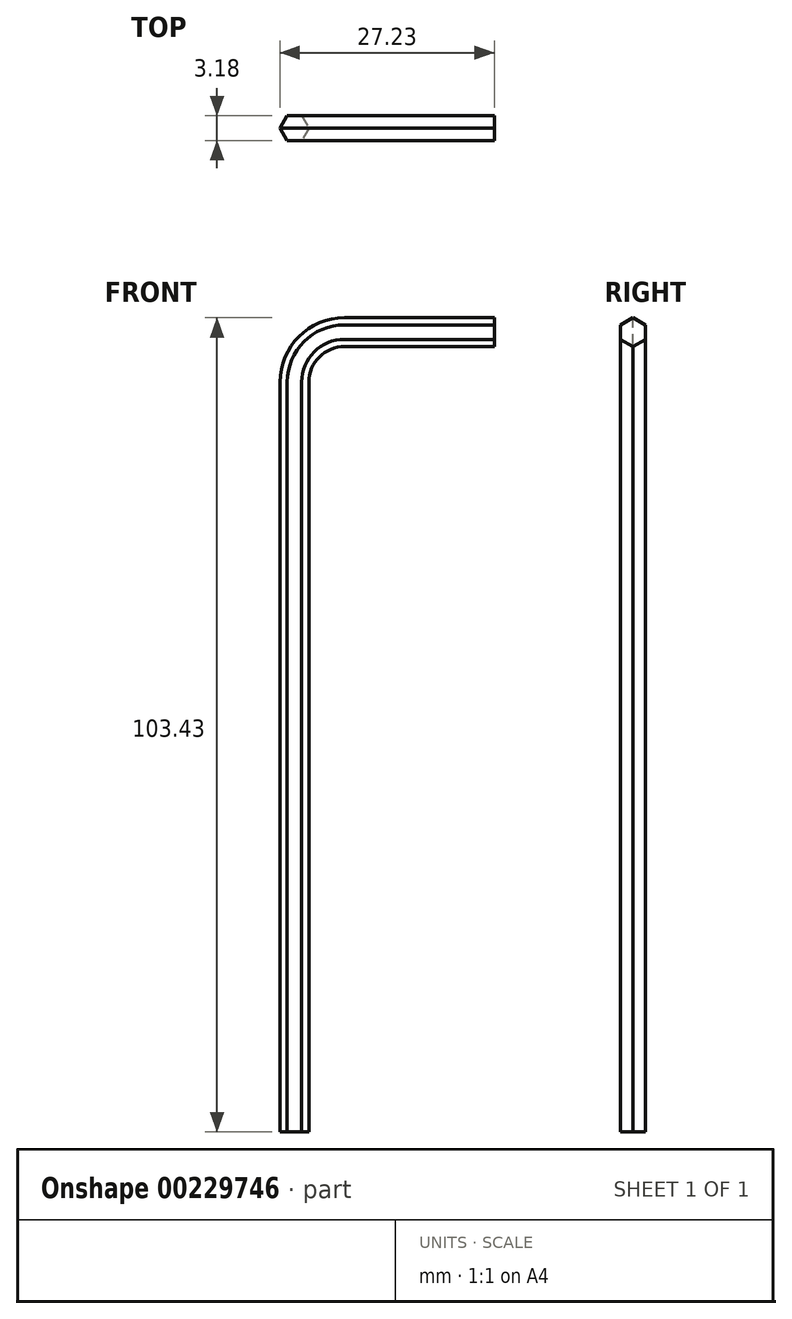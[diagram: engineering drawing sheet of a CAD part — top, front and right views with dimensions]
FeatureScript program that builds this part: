
annotation { "Feature Type Name" : "Feature", "Feature Type Description" : "" }
export const myFeature = defineFeature(function(context is Context, id is Id, definition is map)
    precondition{}
    {
        {
            var Q0;
            Q0=qCreatedBy(makeId("Top.planeOp"),FACE);
            var sketch = newSketch(context, id + "F0", { "sketchPlane" : qUnion([Q0])});
            skCircle(sketch, "E0.cCircle", {"center": v(0, 0) * mm, "radius": 1.59 * mm, "construction": true});
            skLineSegment(sketch, "E0.0", {"start": v(-0.92, 1.59) * mm, "end": v(0.92, 1.59) * mm});
            skLineSegment(sketch, "E0.1", {"start": v(0.92, 1.59) * mm, "end": v(1.83, 0) * mm});
            skLineSegment(sketch, "E0.2", {"start": v(1.83, 0) * mm, "end": v(0.92, -1.59) * mm});
            skLineSegment(sketch, "E0.3", {"start": v(0.92, -1.59) * mm, "end": v(-0.92, -1.59) * mm});
            skLineSegment(sketch, "E0.4", {"start": v(-0.92, -1.59) * mm, "end": v(-1.83, 0) * mm});
            skLineSegment(sketch, "E0.5", {"start": v(-1.83, 0) * mm, "end": v(-0.92, 1.59) * mm});
            skPoint(sketch, "E0.0.midPoint", {"position": v(0, 1.59) * mm});
            skSolve(sketch);
        }
        {
            var Q0;
            Q0=qCreatedBy(makeId("Front.planeOp"),FACE);
            var sketch = newSketch(context, id + "F1", { "sketchPlane" : qUnion([Q0])});
            skLineSegment(sketch, "E1", {"start": v(0, 0) * mm, "end": v(0, 95.25) * mm});
            skLineSegment(sketch, "E2", {"start": v(6.35, 101.6) * mm, "end": v(25.4, 101.6) * mm});
            skPoint(sketch, "E3.visualSharp", {"position": v(0, 101.6) * mm});
            skArc(sketch, "E3.filletArc", {"start": v(6.35, 101.6) * mm, "mid": v(1.86, 99.74) * mm, "end": v(0, 95.25) * mm});
            skSolve(sketch);
        }
        {
            var Q0;
            Q0=makeQuery(id+"F0.imprint","IMPRINT",FACE,{"disambiguationData":[TD([[makeQuery(id+"F0.imprint","IMPRINT",EDGE,{"derivedFrom":sQuery(id+"F0.wireOp",EDGE,"E0.0")}),-1.0]])]});
            var Q1;
            Q1=sQuery(id+"F1.wireOp",EDGE,"E1");
            var Q2;
            Q2=sQuery(id+"F1.wireOp",EDGE,"E3.filletArc");
            var Q3;
            Q3=sQuery(id+"F1.wireOp",EDGE,"E2");
            sweep(context, id + "F2", {"profiles" : qUnion([Q0]), "path" : qUnion([Q1, Q2, Q3])});
        }
    });
